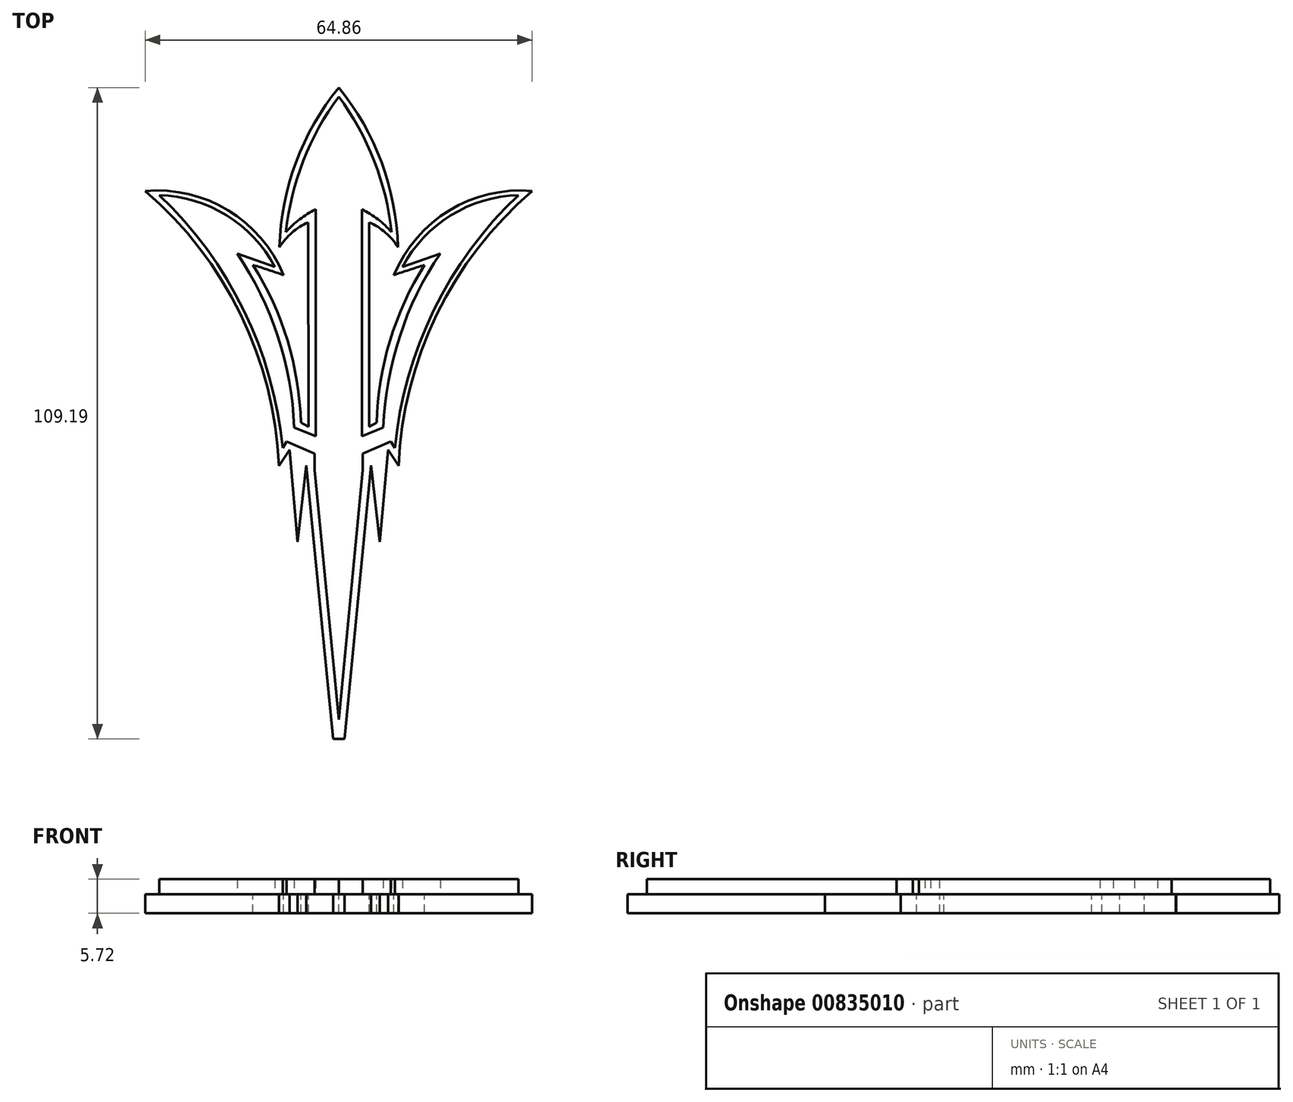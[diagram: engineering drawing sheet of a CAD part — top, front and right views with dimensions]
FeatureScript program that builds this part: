
annotation { "Feature Type Name" : "Feature", "Feature Type Description" : "" }
export const myFeature = defineFeature(function(context is Context, id is Id, definition is map)
    precondition{}
    {
        {
            var Q0;
            Q0=qCreatedBy(makeId("Top.planeOp"),FACE);
            var sketch = newSketch(context, id + "F0", { "sketchPlane" : qUnion([Q0])});
            skArc(sketch, "E0", {"start": v(-10.03, -2.04) * mm, "mid": v(-16.44, 23.33) * mm, "end": v(-32.43, 44.04) * mm});
            skArc(sketch, "E1", {"start": v(-9.24, 29.95) * mm, "mid": v(-18.53, 40.8) * mm, "end": v(-32.43, 44.04) * mm});
            skArc(sketch, "E2", {"start": v(-9.24, 29.95) * mm, "mid": v(-11.8, 30.81) * mm, "end": v(-14.37, 31.64) * mm});
            skArc(sketch, "E3", {"start": v(-6.34, 5.2) * mm, "mid": v(-8.58, 18.96) * mm, "end": v(-14.37, 31.64) * mm});
            skLineSegment(sketch, "E4", {"start": v(-10.03, -2.04) * mm, "end": v(-8.25, 0.64) * mm});
            skLineSegment(sketch, "E5", {"start": v(-8.25, 0.64) * mm, "end": v(-6.9, -14.76) * mm});
            skLineSegment(sketch, "E6", {"start": v(-6.9, -14.76) * mm, "end": v(-5.44, -1.95) * mm});
            skLineSegment(sketch, "E7", {"start": v(-5.44, -1.95) * mm, "end": v(-0.96, -47.8) * mm});
            skLineSegment(sketch, "E8", {"start": v(-0.96, -47.8) * mm, "end": v(0, -47.8) * mm});
            skLineSegment(sketch, "E9", {"start": v(-6.34, 5.2) * mm, "end": v(-5.1, 4.51) * mm});
            skLineSegment(sketch, "E10", {"start": v(-5.1, 4.51) * mm, "end": v(-5.11, 38.79) * mm});
            skArc(sketch, "E11", {"start": v(-5.11, 38.79) * mm, "mid": v(-7.82, 37.07) * mm, "end": v(-9.92, 34.64) * mm});
            skArc(sketch, "E12", {"start": v(0, 61.38) * mm, "mid": v(-7.18, 48.83) * mm, "end": v(-9.92, 34.64) * mm});
            skLineSegment(sketch, "E13.MirrorCS", {"start": v(5.44, -1.95) * mm, "end": v(0.96, -47.8) * mm});
            skLineSegment(sketch, "E14.MirrorCS", {"start": v(0.96, -47.8) * mm, "end": v(0, -47.8) * mm});
            skLineSegment(sketch, "E15.MirrorCS", {"start": v(6.9, -14.76) * mm, "end": v(5.44, -1.95) * mm});
            skLineSegment(sketch, "E16.MirrorCS", {"start": v(8.25, 0.64) * mm, "end": v(6.9, -14.76) * mm});
            skLineSegment(sketch, "E17.MirrorCS", {"start": v(10.03, -2.04) * mm, "end": v(8.25, 0.64) * mm});
            skArc(sketch, "E18.MirrorCS", {"start": v(10.03, -2.04) * mm, "mid": v(16.44, 23.33) * mm, "end": v(32.43, 44.04) * mm});
            skArc(sketch, "E19.MirrorCS", {"start": v(9.24, 29.95) * mm, "mid": v(18.53, 40.8) * mm, "end": v(32.43, 44.04) * mm});
            skArc(sketch, "E20.MirrorCS", {"start": v(6.34, 5.2) * mm, "mid": v(8.58, 18.96) * mm, "end": v(14.37, 31.64) * mm});
            skLineSegment(sketch, "E21.MirrorCS", {"start": v(5.1, 4.51) * mm, "end": v(5.11, 38.79) * mm});
            skArc(sketch, "E22.MirrorCS", {"start": v(0, 61.38) * mm, "mid": v(7.18, 48.83) * mm, "end": v(9.92, 34.64) * mm});
            skArc(sketch, "E23.MirrorCS", {"start": v(5.11, 38.79) * mm, "mid": v(7.82, 37.07) * mm, "end": v(9.92, 34.64) * mm});
            skArc(sketch, "E24.MirrorCS", {"start": v(9.24, 29.95) * mm, "mid": v(11.8, 30.81) * mm, "end": v(14.37, 31.64) * mm});
            skLineSegment(sketch, "E25.MirrorCS", {"start": v(6.34, 5.2) * mm, "end": v(5.1, 4.51) * mm});
            skSolve(sketch);
        }
        {
            var Q0;
            Q0=qCreatedBy(makeId("Top.planeOp"),FACE);
            var sketch = newSketch(context, id + "F1", { "sketchPlane" : qUnion([Q0])});
            skLineSegment(sketch, "E26", {"start": v(-4.04, -2.74) * mm, "end": v(0, -44.58) * mm});
            skLineSegment(sketch, "E27", {"start": v(0, -44.58) * mm, "end": v(-4.04, -2.74) * mm});
            skLineSegment(sketch, "E28", {"start": v(-4.04, 0) * mm, "end": v(-4.04, -2.74) * mm});
            skLineSegment(sketch, "E29", {"start": v(-4.04, 0) * mm, "end": v(-8.75, 2.04) * mm});
            skLineSegment(sketch, "E30", {"start": v(-8.75, 2.04) * mm, "end": v(-9.4, 0.97) * mm});
            skArc(sketch, "E31", {"start": v(-9.4, 0.97) * mm, "mid": v(-15.91, 24.03) * mm, "end": v(-30.09, 43.34) * mm});
            skArc(sketch, "E32", {"start": v(-10.7, 31.34) * mm, "mid": v(-18.78, 39.95) * mm, "end": v(-30.09, 43.34) * mm});
            skLineSegment(sketch, "E33", {"start": v(-10.7, 31.34) * mm, "end": v(-17.02, 33.58) * mm});
            skArc(sketch, "E34", {"start": v(-7.47, 4.43) * mm, "mid": v(-10.21, 19.67) * mm, "end": v(-17.02, 33.58) * mm});
            skLineSegment(sketch, "E35", {"start": v(-7.47, 4.43) * mm, "end": v(-3.87, 2.94) * mm});
            skArc(sketch, "E36", {"start": v(0, 59.87) * mm, "mid": v(-5.95, 49.1) * mm, "end": v(-8.86, 37.14) * mm});
            skLineSegment(sketch, "E37", {"start": v(0, 61.14) * mm, "end": v(0, -46.16) * mm});
            skLineSegment(sketch, "E38", {"start": v(-3.87, 2.94) * mm, "end": v(-3.87, 40.98) * mm});
            skArc(sketch, "E39", {"start": v(-3.87, 40.98) * mm, "mid": v(-6.55, 39.3) * mm, "end": v(-8.86, 37.14) * mm});
            skArc(sketch, "E40.MirrorCS", {"start": v(0, 59.87) * mm, "mid": v(5.95, 49.1) * mm, "end": v(8.86, 37.14) * mm});
            skArc(sketch, "E41.MirrorCS", {"start": v(3.87, 40.98) * mm, "mid": v(6.55, 39.3) * mm, "end": v(8.86, 37.14) * mm});
            skLineSegment(sketch, "E42.MirrorCS", {"start": v(3.87, 2.94) * mm, "end": v(3.87, 40.98) * mm});
            skLineSegment(sketch, "E43.MirrorCS", {"start": v(10.7, 31.34) * mm, "end": v(17.02, 33.58) * mm});
            skArc(sketch, "E44.MirrorCS", {"start": v(10.7, 31.34) * mm, "mid": v(18.78, 39.95) * mm, "end": v(30.09, 43.34) * mm});
            skArc(sketch, "E45.MirrorCS", {"start": v(7.47, 4.43) * mm, "mid": v(10.21, 19.67) * mm, "end": v(17.02, 33.58) * mm});
            skArc(sketch, "E46.MirrorCS", {"start": v(9.4, 0.97) * mm, "mid": v(15.91, 24.03) * mm, "end": v(30.09, 43.34) * mm});
            skLineSegment(sketch, "E47.MirrorCS", {"start": v(7.47, 4.43) * mm, "end": v(3.87, 2.94) * mm});
            skLineSegment(sketch, "E48.MirrorCS", {"start": v(4.04, 0) * mm, "end": v(8.75, 2.04) * mm});
            skLineSegment(sketch, "E49.MirrorCS", {"start": v(4.04, 0) * mm, "end": v(4.04, -2.74) * mm});
            skLineSegment(sketch, "E50.MirrorCS", {"start": v(4.04, -2.74) * mm, "end": v(0, -44.58) * mm});
            skLineSegment(sketch, "E51.MirrorCS", {"start": v(8.75, 2.04) * mm, "end": v(9.4, 0.97) * mm});
            skSolve(sketch);
        }
        {
            var Q0;
            Q0 = qSketchRegion(id + "F0", true);
            extrude(context, id + "F2", {"entities" : qUnion([Q0]), "depth" : 3.17 * mm, "offsetDistance" : 25.4 * mm});
        }
        {
            var Q0;
            Q0 = qSketchRegion(id + "F1", true);
            extrude(context, id + "F3", {"entities" : qUnion([Q0]), "depth" : 2.54 * mm, "offsetDistance" : 25.4 * mm});
        }
        {
            var Q0;
            Q0=makeQuery(id+"F2.opExtrude","SWEPT_BODY",BODY,{"disambiguationData":[OSD([sQuery(id+"F0.wireOp",EDGE,"E0"),sQuery(id+"F0.wireOp",EDGE,"E1"),sQuery(id+"F0.wireOp",EDGE,"E2"),sQuery(id+"F0.wireOp",EDGE,"E3"),sQuery(id+"F0.wireOp",EDGE,"E4"),sQuery(id+"F0.wireOp",EDGE,"E5"),sQuery(id+"F0.wireOp",EDGE,"E6"),sQuery(id+"F0.wireOp",EDGE,"E7"),sQuery(id+"F0.wireOp",EDGE,"E8"),sQuery(id+"F0.wireOp",EDGE,"E9"),sQuery(id+"F0.wireOp",EDGE,"E10"),sQuery(id+"F0.wireOp",EDGE,"E11"),sQuery(id+"F0.wireOp",EDGE,"E12"),sQuery(id+"F0.wireOp",EDGE,"E13.MirrorCS"),sQuery(id+"F0.wireOp",EDGE,"E14.MirrorCS"),sQuery(id+"F0.wireOp",EDGE,"E15.MirrorCS"),sQuery(id+"F0.wireOp",EDGE,"E16.MirrorCS"),sQuery(id+"F0.wireOp",EDGE,"E17.MirrorCS"),sQuery(id+"F0.wireOp",EDGE,"E18.MirrorCS"),sQuery(id+"F0.wireOp",EDGE,"E19.MirrorCS"),sQuery(id+"F0.wireOp",EDGE,"E20.MirrorCS"),sQuery(id+"F0.wireOp",EDGE,"E21.MirrorCS"),sQuery(id+"F0.wireOp",EDGE,"E22.MirrorCS"),sQuery(id+"F0.wireOp",EDGE,"E23.MirrorCS"),sQuery(id+"F0.wireOp",EDGE,"E24.MirrorCS"),sQuery(id+"F0.wireOp",EDGE,"E25.MirrorCS")])]});
            var Q1;
            Q1=sQuery(id+"F1.wireOp",EDGE,"E37");
            transform(context, id + "F4", {"entities" : qUnion([Q0]), "transformType" : TransformType.ROTATION, "transformAxis" : qUnion([Q1]), "angle" : 180 * degree, "makeCopy" : false});
        }
    });
